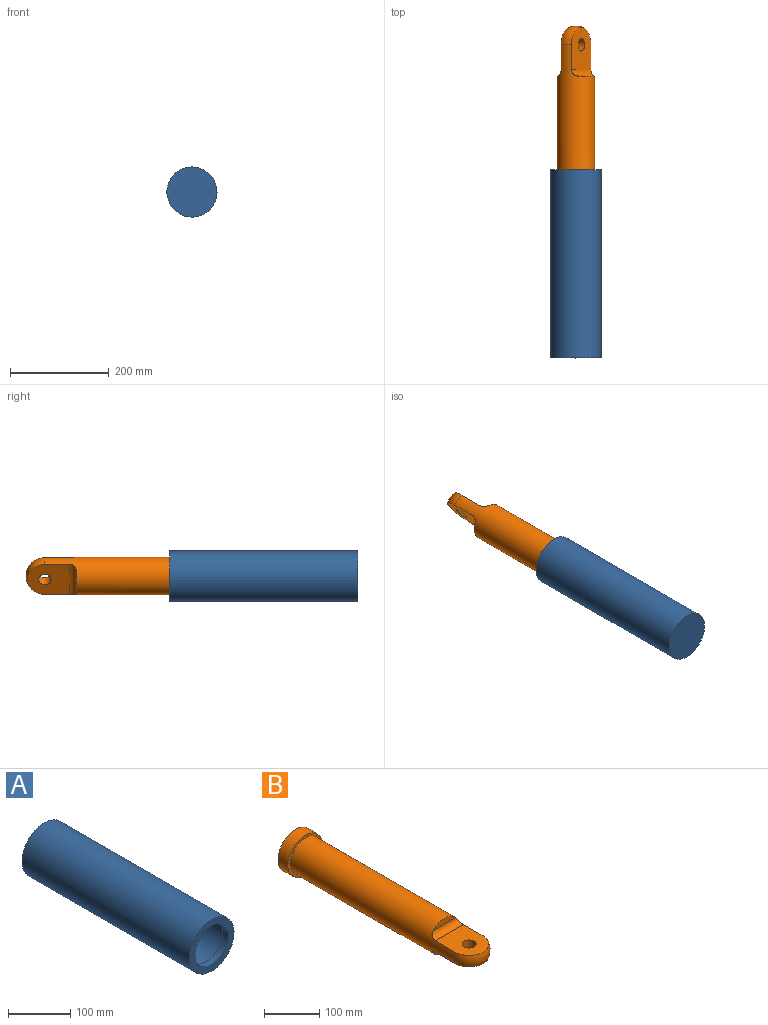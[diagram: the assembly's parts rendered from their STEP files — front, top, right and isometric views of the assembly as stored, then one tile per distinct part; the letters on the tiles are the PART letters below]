
ASSEMBLY  parts=2 mates=1
PART A: 7 faces, bbox 101.6x381x101.6 mm
  f0: plane 88.9x88.9mm, normal (0,1,0), area 1646.8mm2, adj f1,f4
  f1: cylinder r=38.1mm len=76.2mm, axis (0,1,0), area 3040.2mm2, adj f0,f3
  f2: cylinder r=50.8mm len=381mm, axis (0,1,0), area 121609.8mm2, adj f3,f6
  f3: plane 101.6x101.6mm, normal (0,-1,0), area 3547mm2, adj f1,f2
  f4: cylinder r=44.45mm len=355.6mm, axis (0,-1,0), area 99314.7mm2, adj f0,f5
  f5: plane 88.9x88.9mm, normal (0,-1,0), area 6207.2mm2, adj f4
  f6: plane 101.6x101.6mm, normal (0,1,0), area 8107.3mm2, adj f2
PART B: 12 faces, bbox 88.9x482.6x88.9 mm
  f0: cylinder r=44.45mm len=88.9mm, axis (0,1,0), area 7093.9mm2, adj f1,f2
  f1: plane 88.9x88.9mm, normal (0,-1,0), area 1646.8mm2, adj f0,f3
  f2: plane 88.9x88.9mm, normal (0,1,0), area 6207.2mm2, adj f0
  f3: cylinder r=38.1mm len=419.1mm, axis (0,1,0), area 88568mm2, adj f1,f4,f5,f6,f7,f8,f9,f10
  f4: plane 86.72x71.84mm, normal (0,0,-1), area 5169.7mm2, adj f3,f8,f9,f11
  f5: plane 56.8x12.7mm, normal (0,-1,0), area 499.6mm2, adj f3,f9
  f6: plane 86.72x71.84mm, normal (0,0,1), area 5169.7mm2, adj f3,f8,f10,f11
  f7: plane 56.8x12.7mm, normal (0,-1,0), area 499.6mm2, adj f3,f10
  f8: sphere r=38.1mm, area 3040.2mm2, adj f3,f4,f6
  f9: cylinder r=12.7mm len=71.84mm, axis (-1,0,0), area 1342.2mm2, adj f3,f4,f5
  f10: cylinder r=12.7mm len=71.84mm, axis (1,0,0), area 1342.2mm2, adj f3,f6,f7
  f11: cylinder r=12.7mm len=25.4mm, axis (0,0,1), area 2026.8mm2, adj f4,f6
PLACE A rot(axis=(-0.29,0,0.96),180deg) t=(-589.04,-486.66,-347.24)mm
PLACE B rot(axis=(0.48,0,0.88),180deg) t=(-589.04,-664.86,-347.24)mm
MATE slider B.f3 <-> A.f2  axis (0,-1,0) through (-589.04,-429.91,-347.24)mm
